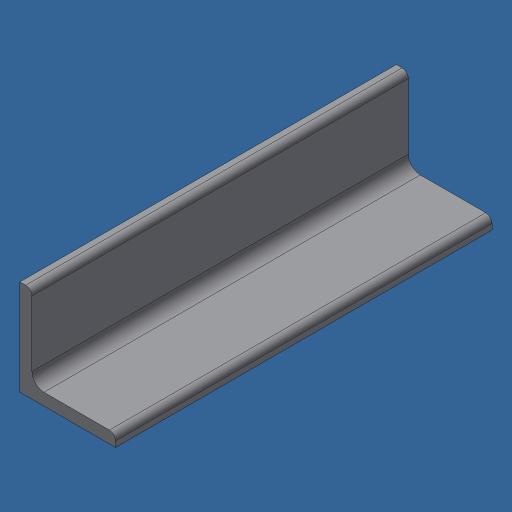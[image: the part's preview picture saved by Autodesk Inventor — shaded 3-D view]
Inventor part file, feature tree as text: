
AUTODESK INVENTOR PART (.ipt)
format: ipt  version: 2024.3 (Build 283343000, 343)  size: 111,616 bytes
history: native  units: mm (DEFAULTED — no unit token found)
features: other x1, extrude x1
ambient origin geometry x8: Origin, YZ Plane, XZ Plane, XY Plane, X Axis, Y Axis, Z Axis, Center Point
bodies: Body1 (feature_tree)
feature tree (2):
  other  "Finish - None"
  extrude  "1" X 1" X 1/8""  Depth=3.175mm
